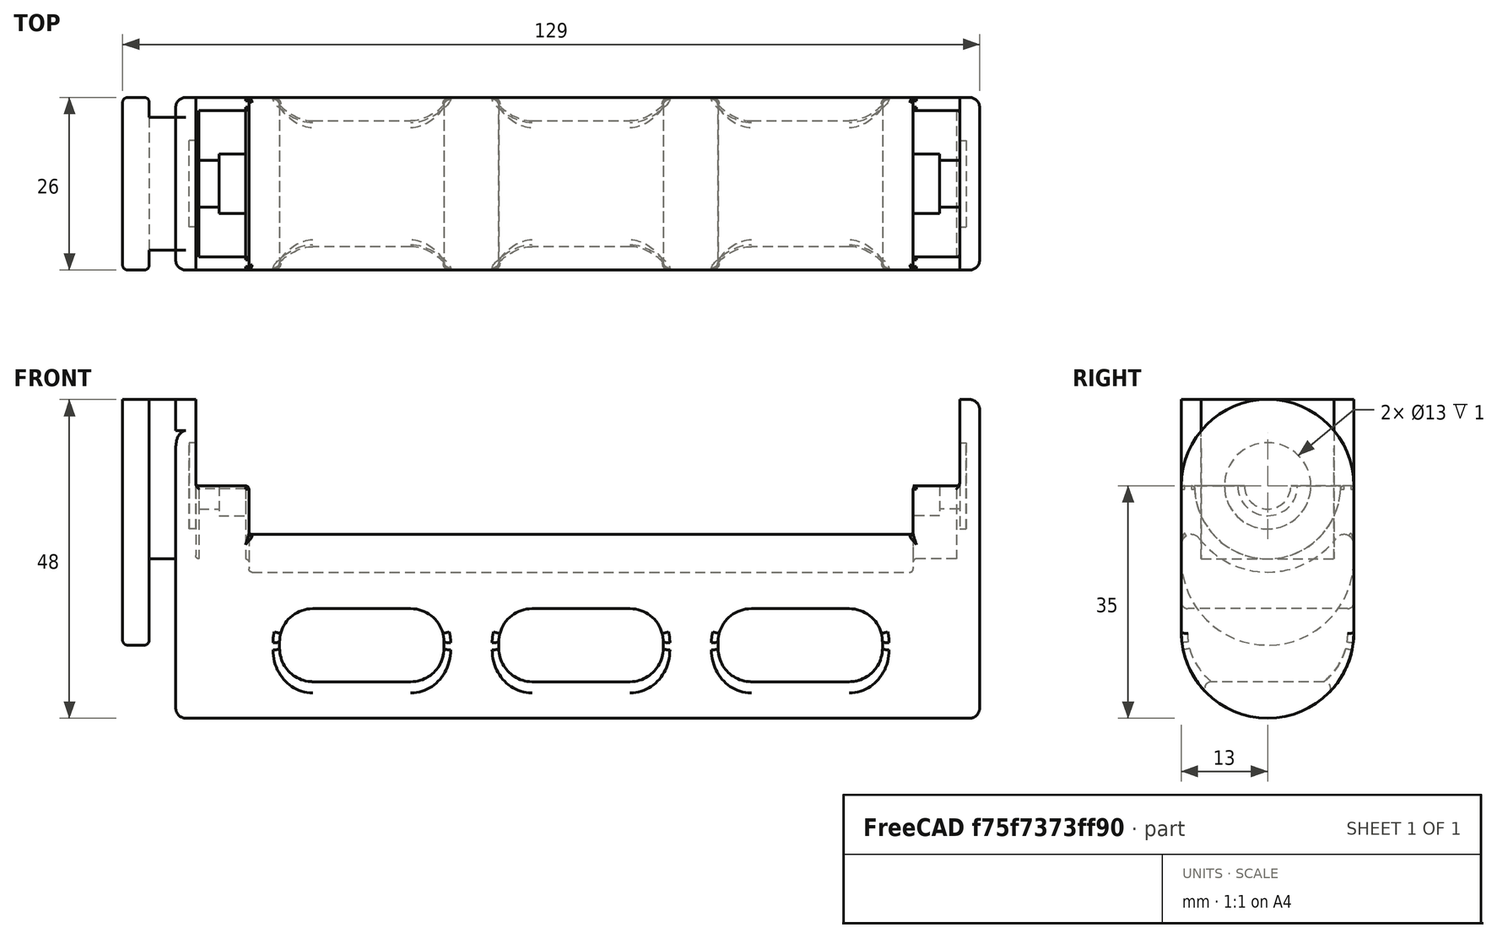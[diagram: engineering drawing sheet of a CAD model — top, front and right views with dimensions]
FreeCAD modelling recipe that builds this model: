
FCSTD DOCUMENT  (FreeCAD 0.18R16146 (Git))
Label: FillerBraceSource
License: All rights reserved
LicenseURL: http://en.wikipedia.org/wiki/All_rights_reserved
objects: Part::Cut×4, Part::Cylinder×3, Part::Fuse×2, Part::Feature×1, Part::Box×1
note: 11 computed .brp shape members not serialized (recipe doc carries the construction recipe); baked Part::Feature solids carry a one-line shape summary decoded from their .brp

FEATURE [Part::Feature] Part__Feature  label="FilamentHolder3dpnFinal v21"
  shape: bbox 129 x 28.15 x 50.15 mm, 184 faces (baked)
FEATURE [Part::Cylinder] Cylinder
  Angle = 360
  AttacherType = Attacher::AttachEngine3D
  Height = 7
  Radius = 11
FEATURE [Part::Box] Box  label="Cube"
  AttacherType = Attacher::AttachEngine3D
  Height = 7
  Length = 11
  Placement = pos=(0,-11,0) rot=(0,0,1;0rad)
  Width = 22
FEATURE [Part::Cylinder] Cylinder001
  Angle = 360
  AttacherType = Attacher::AttachEngine3D
  Height = 3
  Radius = 3.5
FEATURE [Part::Cut] Cut
  Base = -> Cylinder
  Tool = -> Cylinder001
FEATURE [Part::Cylinder] Cylinder002
  Angle = 360
  AttacherType = Attacher::AttachEngine3D
  Height = 10
  Placement = pos=(0,0,3) rot=(0,0,1;0rad)
  Radius = 4.5
FEATURE [Part::Cut] Cut001
  Base = -> Cut
  Tool = -> Cylinder002
FEATURE [Part::Cut] Cut002
  Base = -> Cut001
  Placement = pos=(11.5,-1.4e-15,35) rot=(-0.707107,0,-0.707107;3.14159rad)
  Tool = -> Box
FEATURE [Part::Cut] Cut003
  Base = -> Cut001
  Placement = pos=(126,0,35) rot=(0,-1,0;1.5708rad)
  Tool = -> Box
FEATURE [Part::Fuse] Fusion
  Base = -> Part__Feature
  Tool = -> Cut003
FEATURE [Part::Fuse] Fusion001
  Base = -> Cut002
  Tool = -> Fusion
